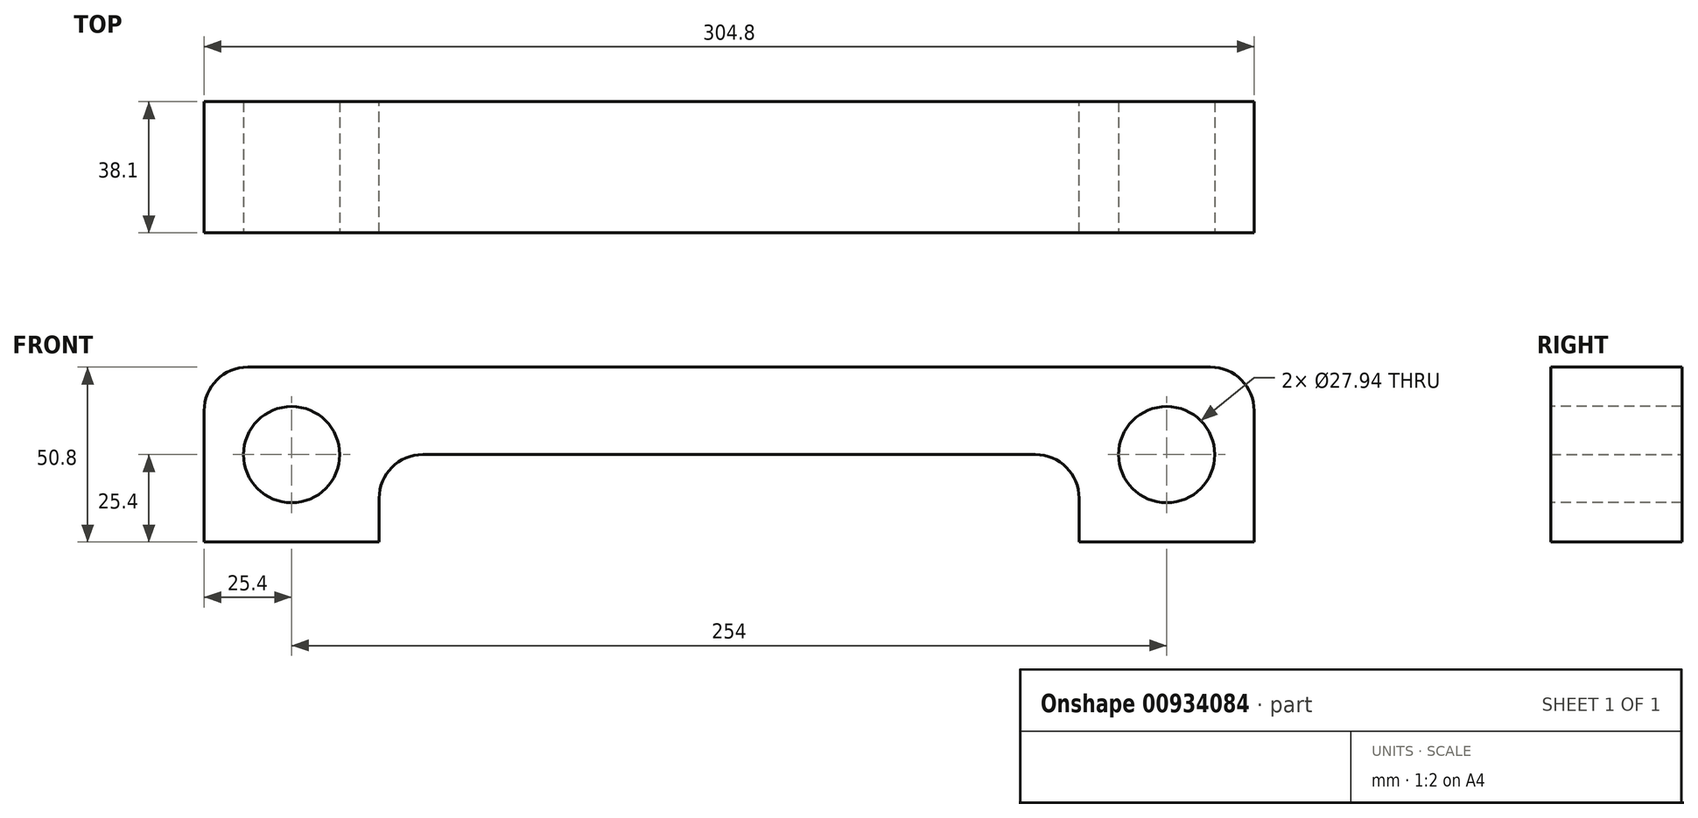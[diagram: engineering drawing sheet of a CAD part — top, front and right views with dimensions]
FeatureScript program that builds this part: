
annotation { "Feature Type Name" : "Feature", "Feature Type Description" : "" }
export const myFeature = defineFeature(function(context is Context, id is Id, definition is map)
    precondition{}
    {
        {
            var Q0;
            Q0=qCreatedBy(makeId("Front.planeOp"),FACE);
            var sketch = newSketch(context, id + "F0", { "sketchPlane" : qUnion([Q0])});
            skLineSegment(sketch, "E0.bottom", {"start": v(-139.7, 25.4) * mm, "end": v(139.7, 25.4) * mm});
            skLineSegment(sketch, "E0.top", {"start": v(-152.4, -25.4) * mm, "end": v(-101.6, -25.4) * mm});
            skLineSegment(sketch, "E0.left", {"start": v(-152.4, 12.7) * mm, "end": v(-152.4, -25.4) * mm});
            skLineSegment(sketch, "E0.right", {"start": v(152.4, 12.7) * mm, "end": v(152.4, -25.4) * mm});
            skLineSegment(sketch, "E1", {"start": v(-101.6, -25.4) * mm, "end": v(-101.6, -12.7) * mm});
            skPoint(sketch, "E1.endSnap0", {"position": v(-152.4, 0) * mm});
            skLineSegment(sketch, "E2", {"start": v(-88.9, 0) * mm, "end": v(88.9, 0) * mm});
            skLineSegment(sketch, "E3", {"start": v(101.6, -12.7) * mm, "end": v(101.6, -25.4) * mm});
            skPoint(sketch, "E4.visualSharp", {"position": v(-101.6, 0) * mm});
            skArc(sketch, "E4.filletArc", {"start": v(-88.9, 0) * mm, "mid": v(-97.88, -3.72) * mm, "end": v(-101.6, -12.7) * mm});
            skPoint(sketch, "E5.visualSharp", {"position": v(-152.4, 25.4) * mm});
            skArc(sketch, "E5.filletArc", {"start": v(-139.7, 25.4) * mm, "mid": v(-148.68, 21.68) * mm, "end": v(-152.4, 12.7) * mm});
            skPoint(sketch, "E6.visualSharp", {"position": v(101.6, 0) * mm});
            skArc(sketch, "E6.filletArc", {"start": v(101.6, -12.7) * mm, "mid": v(97.88, -3.72) * mm, "end": v(88.9, 0) * mm});
            skPoint(sketch, "E7.visualSharp", {"position": v(152.4, 25.4) * mm});
            skArc(sketch, "E7.filletArc", {"start": v(152.4, 12.7) * mm, "mid": v(148.68, 21.68) * mm, "end": v(139.7, 25.4) * mm});
            skLineSegment(sketch, "E8.trimOffspring", {"start": v(101.6, -25.4) * mm, "end": v(152.4, -25.4) * mm});
            skSolve(sketch);
        }
        {
            var Q0;
            Q0=makeQuery(id+"F0.imprint","IMPRINT",FACE,{"disambiguationData":[TD([[makeQuery(id+"F0.imprint","IMPRINT",EDGE,{"derivedFrom":sQuery(id+"F0.wireOp",EDGE,"E0.bottom")}),-1.0]])]});
            extrude(context, id + "F1", {"entities" : qUnion([Q0]), "depth" : 38.1 * mm, "offsetDistance" : 25.4 * mm});
        }
        {
            var Q0;
            Q0=makeQuery(id+"F1.opExtrude","CAP_FACE",FACE,{"disambiguationData":[OSD([sQuery(id+"F0.wireOp",EDGE,"E0.bottom"),sQuery(id+"F0.wireOp",EDGE,"E0.top"),sQuery(id+"F0.wireOp",EDGE,"E0.left"),sQuery(id+"F0.wireOp",EDGE,"E0.right"),sQuery(id+"F0.wireOp",EDGE,"E1"),sQuery(id+"F0.wireOp",EDGE,"E2"),sQuery(id+"F0.wireOp",EDGE,"E3"),sQuery(id+"F0.wireOp",EDGE,"E4.filletArc"),sQuery(id+"F0.wireOp",EDGE,"E5.filletArc"),sQuery(id+"F0.wireOp",EDGE,"E6.filletArc"),sQuery(id+"F0.wireOp",EDGE,"E7.filletArc"),sQuery(id+"F0.wireOp",EDGE,"E8.trimOffspring")])],"isStart":false});
            var sketch = newSketch(context, id + "F2", { "sketchPlane" : qUnion([Q0])});
            skCircle(sketch, "E9", {"center": v(-127, 0) * mm, "radius": 13.97 * mm});
            skCircle(sketch, "E10", {"center": v(127, 0) * mm, "radius": 13.97 * mm});
            skSolve(sketch);
        }
        {
            var Q0;
            Q0 = qSketchRegion(id + "F2", true);
            extrude(context, id + "F3", {"entities" : qUnion([Q0]), "operationType" : NewBodyOperationType.REMOVE, "endBound" : BoundingType.THROUGH_ALL, "oppositeDirection" : true, "depth" : 25.4 * mm, "offsetDistance" : 25.4 * mm});
        }
    });
